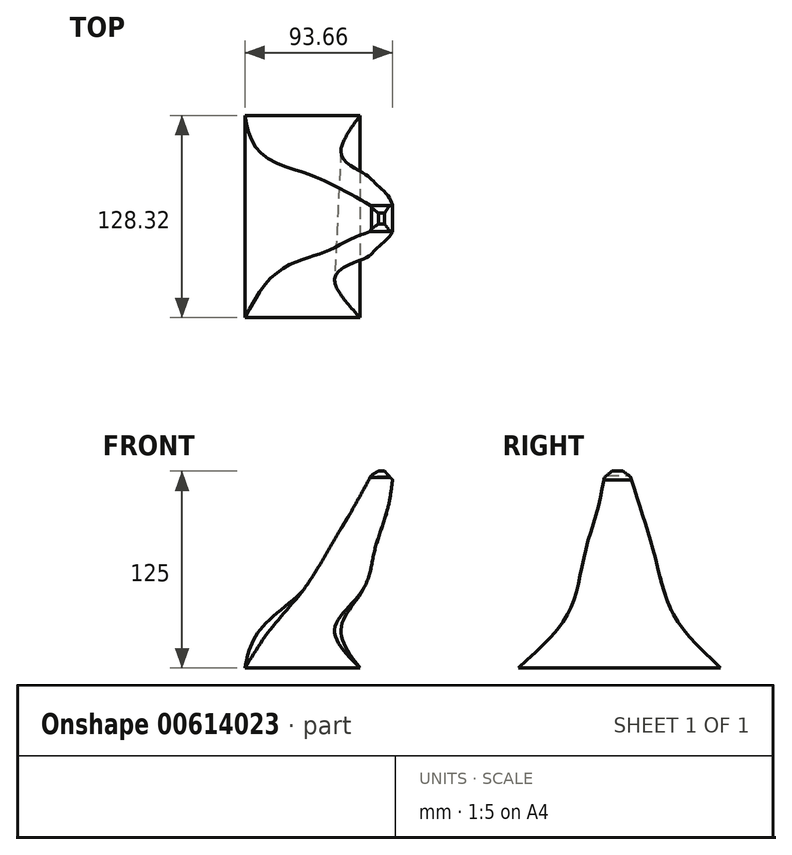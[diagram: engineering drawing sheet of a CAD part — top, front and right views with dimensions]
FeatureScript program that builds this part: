
annotation { "Feature Type Name" : "Feature", "Feature Type Description" : "" }
export const myFeature = defineFeature(function(context is Context, id is Id, definition is map)
    precondition{}
    {
        {
            var Q0;
            Q0=qCreatedBy(makeId("Top.planeOp"),FACE);
            var sketch = newSketch(context, id + "F0", { "sketchPlane" : qUnion([Q0])});
            skLineSegment(sketch, "E0.bottom", {"start": v(-56.59, 86.01) * mm, "end": v(63.41, 86.01) * mm});
            skLineSegment(sketch, "E0.top", {"start": v(-56.59, -83.99) * mm, "end": v(63.41, -83.99) * mm});
            skLineSegment(sketch, "E0.left", {"start": v(-56.59, 86.01) * mm, "end": v(-56.59, -83.99) * mm});
            skLineSegment(sketch, "E0.right", {"start": v(63.41, 86.01) * mm, "end": v(63.41, -83.99) * mm});
            skSolve(sketch);
        }
        {
            var Q0;
            Q0=makeQuery(id+"F0.imprint","IMPRINT",FACE,{"disambiguationData":[TD([[makeQuery(id+"F0.imprint","IMPRINT",EDGE,{"derivedFrom":sQuery(id+"F0.wireOp",EDGE,"E0.bottom")}),-1.0]])]});
            cPlane(context, id + "F1", {"entities" : qUnion([Q0]), "cplaneType" : CPlaneType.OFFSET, "offset" : 25 * mm, "width" : 150 * mm, "height" : 150 * mm});
        }
        {
            var Q0;
            Q0=qCreatedBy(id+"F1.planeOp",FACE);
            var sketch = newSketch(context, id + "F2", { "sketchPlane" : qUnion([Q0])});
            skLineSegment(sketch, "E1.bottom", {"start": v(-37.4, 71.22) * mm, "end": v(35.65, 71.22) * mm});
            skLineSegment(sketch, "E1.top", {"start": v(-37.4, -57.1) * mm, "end": v(35.65, -57.1) * mm});
            skLineSegment(sketch, "E1.left", {"start": v(-37.4, 71.22) * mm, "end": v(-37.4, -57.1) * mm});
            skLineSegment(sketch, "E1.right", {"start": v(35.65, 71.22) * mm, "end": v(35.65, -57.1) * mm});
            skSolve(sketch);
        }
        {
            var Q0;
            Q0=makeQuery(id+"F2.imprint","IMPRINT",FACE,{"disambiguationData":[TD([[makeQuery(id+"F2.imprint","IMPRINT",EDGE,{"derivedFrom":sQuery(id+"F2.wireOp",EDGE,"E1.bottom")}),-1.0]])]});
            cPlane(context, id + "F3", {"entities" : qUnion([Q0]), "cplaneType" : CPlaneType.OFFSET, "offset" : 25 * mm, "width" : 150 * mm, "height" : 150 * mm});
        }
        {
            var Q0;
            Q0=qCreatedBy(id+"F3.planeOp",FACE);
            var sketch = newSketch(context, id + "F4", { "sketchPlane" : qUnion([Q0])});
            skLineSegment(sketch, "E2", {"start": v(0, 0) * mm, "end": v(23.56, 47.28) * mm});
            skLineSegment(sketch, "E3", {"start": v(23.56, 47.28) * mm, "end": v(-27.28, 47.28) * mm});
            skLineSegment(sketch, "E4", {"start": v(-27.28, 47.28) * mm, "end": v(0, 0) * mm});
            skLineSegment(sketch, "E5", {"start": v(0, 0) * mm, "end": v(-20.86, -31.93) * mm});
            skLineSegment(sketch, "E6", {"start": v(-20.86, -31.93) * mm, "end": v(19.61, -31.93) * mm});
            skLineSegment(sketch, "E7", {"start": v(19.61, -31.93) * mm, "end": v(0, 0) * mm});
            skLineSegment(sketch, "E8", {"start": v(-20.86, -31.93) * mm, "end": v(-27.28, 47.28) * mm});
            skLineSegment(sketch, "E9", {"start": v(23.56, 47.28) * mm, "end": v(19.61, -31.93) * mm});
            skSolve(sketch);
        }
        {
            var Q0;
            Q0=qCreatedBy(id+"F3.planeOp",FACE);
            cPlane(context, id + "F5", {"entities" : qUnion([Q0]), "cplaneType" : CPlaneType.OFFSET, "offset" : 25 * mm, "width" : 150 * mm, "height" : 150 * mm});
        }
        {
            var Q0;
            Q0=qCreatedBy(id+"F5.planeOp",FACE);
            var sketch = newSketch(context, id + "F6", { "sketchPlane" : qUnion([Q0])});
            skLineSegment(sketch, "E10", {"start": v(0, -19.84) * mm, "end": v(0, 34.95) * mm});
            skLineSegment(sketch, "E11", {"start": v(0, 34.95) * mm, "end": v(37.62, 34.95) * mm});
            skLineSegment(sketch, "E12", {"start": v(37.62, 34.95) * mm, "end": v(37.62, -19.84) * mm});
            skLineSegment(sketch, "E13", {"start": v(0, -19.84) * mm, "end": v(37.62, -19.84) * mm});
            skSolve(sketch);
        }
        {
            var Q0;
            Q0=qCreatedBy(id+"F5.planeOp",FACE);
            cPlane(context, id + "F7", {"entities" : qUnion([Q0]), "cplaneType" : CPlaneType.OFFSET, "offset" : 25 * mm, "width" : 150 * mm, "height" : 150 * mm});
        }
        {
            var Q0;
            Q0=qCreatedBy(id+"F7.planeOp",FACE);
            var sketch = newSketch(context, id + "F8", { "sketchPlane" : qUnion([Q0])});
            skLineSegment(sketch, "E14.bottom", {"start": v(15.66, 28.53) * mm, "end": v(45.03, 28.53) * mm});
            skLineSegment(sketch, "E14.top", {"start": v(15.66, -14.4) * mm, "end": v(45.03, -14.4) * mm});
            skLineSegment(sketch, "E14.left", {"start": v(15.66, 28.53) * mm, "end": v(15.66, -14.4) * mm});
            skLineSegment(sketch, "E14.right", {"start": v(45.03, 28.53) * mm, "end": v(45.03, -14.4) * mm});
            skSolve(sketch);
        }
        {
            var Q0;
            Q0=qCreatedBy(id+"F7.planeOp",FACE);
            cPlane(context, id + "F9", {"entities" : qUnion([Q0]), "cplaneType" : CPlaneType.OFFSET, "offset" : 25 * mm, "width" : 150 * mm, "height" : 150 * mm});
        }
        {
            var Q0;
            Q0=qCreatedBy(id+"F9.planeOp",FACE);
            var sketch = newSketch(context, id + "F10", { "sketchPlane" : qUnion([Q0])});
            skLineSegment(sketch, "E15.bottom", {"start": v(30.47, 20.88) * mm, "end": v(52.92, 20.88) * mm});
            skLineSegment(sketch, "E15.top", {"start": v(30.47, -7) * mm, "end": v(52.92, -7) * mm});
            skLineSegment(sketch, "E15.left", {"start": v(30.47, 20.88) * mm, "end": v(30.47, -7) * mm});
            skLineSegment(sketch, "E15.right", {"start": v(52.92, 20.88) * mm, "end": v(52.92, -7) * mm});
            skSolve(sketch);
        }
        {
            var Q0;
            Q0=qCreatedBy(id+"F9.planeOp",FACE);
            cPlane(context, id + "F11", {"entities" : qUnion([Q0]), "cplaneType" : CPlaneType.OFFSET, "offset" : 25 * mm, "width" : 150 * mm, "height" : 150 * mm});
        }
        {
            var Q0;
            Q0=qCreatedBy(id+"F11.planeOp",FACE);
            var sketch = newSketch(context, id + "F12", { "sketchPlane" : qUnion([Q0])});
            skLineSegment(sketch, "E16.bottom", {"start": v(44.29, 12.98) * mm, "end": v(56.87, 12.98) * mm});
            skLineSegment(sketch, "E16.top", {"start": v(44.29, -1.82) * mm, "end": v(56.87, -1.82) * mm});
            skLineSegment(sketch, "E16.left", {"start": v(44.29, 12.98) * mm, "end": v(44.29, -1.82) * mm});
            skLineSegment(sketch, "E16.right", {"start": v(56.87, 12.98) * mm, "end": v(56.87, -1.82) * mm});
            skSolve(sketch);
        }
        {
            var Q0;
            Q0=makeQuery(id+"F2.imprint","IMPRINT",FACE,{"disambiguationData":[TD([[makeQuery(id+"F2.imprint","IMPRINT",EDGE,{"derivedFrom":sQuery(id+"F2.wireOp",EDGE,"E1.bottom")}),-1.0]])]});
            var Q1;
            Q1 = qSketchRegion(id + "F4", true);
            var Q2;
            Q2 = qSketchRegion(id + "F6", true);
            var Q3;
            Q3 = qSketchRegion(id + "F8", true);
            var Q4;
            Q4 = qSketchRegion(id + "F10", true);
            var Q5;
            Q5 = qSketchRegion(id + "F12", true);
            loft(context, id + "F13", {"sheetProfilesArray" : [{ "sheetProfileEntities" : qUnion([Q0]) }, { "sheetProfileEntities" : qUnion([Q1]) }, { "sheetProfileEntities" : qUnion([Q2]) }, { "sheetProfileEntities" : qUnion([Q3]) }, { "sheetProfileEntities" : qUnion([Q4]) }, { "sheetProfileEntities" : qUnion([Q5]) }]});
        }
        {
            var Q0;
            Q0=makeQuery(id+"F13.opLoft","MID_CAP_EDGE",EDGE,{"disambiguationData":[OSD([sQuery(id+"F12.wireOp",EDGE,"E16.bottom"),sQuery(id+"F12.wireOp",EDGE,"E16.left"),sQuery(id+"F12.wireOp",EDGE,"E16.right")])],"capPos":5.0});
            var Q1;
            Q1=makeQuery(id+"F13.opLoft","MID_CAP_EDGE",EDGE,{"disambiguationData":[OSD([sQuery(id+"F12.wireOp",EDGE,"E16.bottom"),sQuery(id+"F12.wireOp",EDGE,"E16.top"),sQuery(id+"F12.wireOp",EDGE,"E16.left")])],"capPos":5.0});
            var Q2;
            Q2=makeQuery(id+"F13.opLoft","MID_CAP_EDGE",EDGE,{"disambiguationData":[OSD([sQuery(id+"F12.wireOp",EDGE,"E16.top"),sQuery(id+"F12.wireOp",EDGE,"E16.left"),sQuery(id+"F12.wireOp",EDGE,"E16.right")])],"capPos":5.0});
            var Q3;
            Q3=makeQuery(id+"F13.opLoft","MID_CAP_EDGE",EDGE,{"disambiguationData":[OSD([sQuery(id+"F12.wireOp",EDGE,"E16.bottom"),sQuery(id+"F12.wireOp",EDGE,"E16.top"),sQuery(id+"F12.wireOp",EDGE,"E16.right")])],"capPos":5.0});
            chamfer(context, id + "F14", {"entities" : qUnion([Q0, Q1, Q2, Q3]), "width" : 5 * mm, "tangentPropagation" : true});
        }
    });
